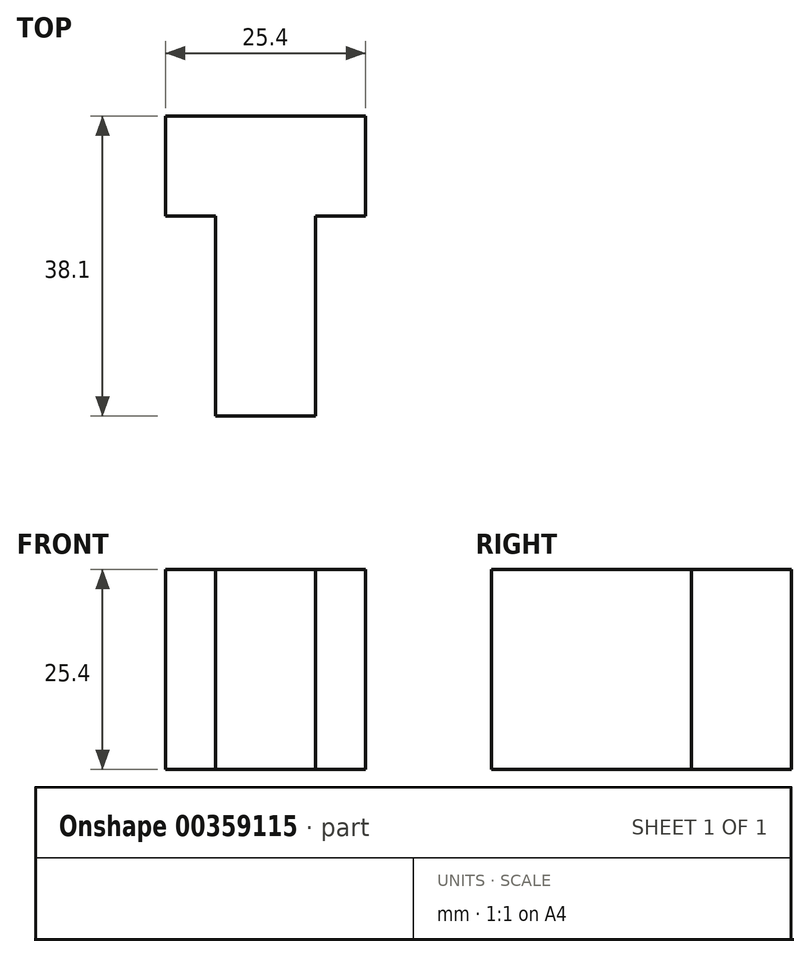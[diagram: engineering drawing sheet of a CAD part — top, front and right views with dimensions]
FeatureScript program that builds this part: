
annotation { "Feature Type Name" : "Feature", "Feature Type Description" : "" }
export const myFeature = defineFeature(function(context is Context, id is Id, definition is map)
    precondition{}
    {
        {
            var Q0;
            Q0=qCreatedBy(makeId("Top.planeOp"),FACE);
            var sketch = newSketch(context, id + "F0", { "sketchPlane" : qUnion([Q0])});
            skLineSegment(sketch, "E0", {"start": v(0, 0) * mm, "end": v(12.7, 0) * mm});
            skLineSegment(sketch, "E1", {"start": v(12.7, 0) * mm, "end": v(12.7, 25.4) * mm});
            skLineSegment(sketch, "E2", {"start": v(12.7, 25.4) * mm, "end": v(19.05, 25.4) * mm});
            skLineSegment(sketch, "E3", {"start": v(19.05, 25.4) * mm, "end": v(19.05, 38.1) * mm});
            skLineSegment(sketch, "E4", {"start": v(19.05, 38.1) * mm, "end": v(-6.35, 38.1) * mm});
            skLineSegment(sketch, "E5", {"start": v(-6.35, 38.1) * mm, "end": v(-6.35, 25.4) * mm});
            skLineSegment(sketch, "E6", {"start": v(-6.35, 25.4) * mm, "end": v(0, 25.4) * mm});
            skLineSegment(sketch, "E7", {"start": v(0, 25.4) * mm, "end": v(0, 0) * mm});
            skSolve(sketch);
        }
        {
            var Q0;
            Q0=makeQuery(id+"F0.imprint","IMPRINT",FACE,{"disambiguationData":[TD([[makeQuery(id+"F0.imprint","IMPRINT",EDGE,{"derivedFrom":sQuery(id+"F0.wireOp",EDGE,"E0")}),1.0]])]});
            extrude(context, id + "F1", {"entities" : qUnion([Q0]), "depth" : 25.4 * mm});
        }
    });
